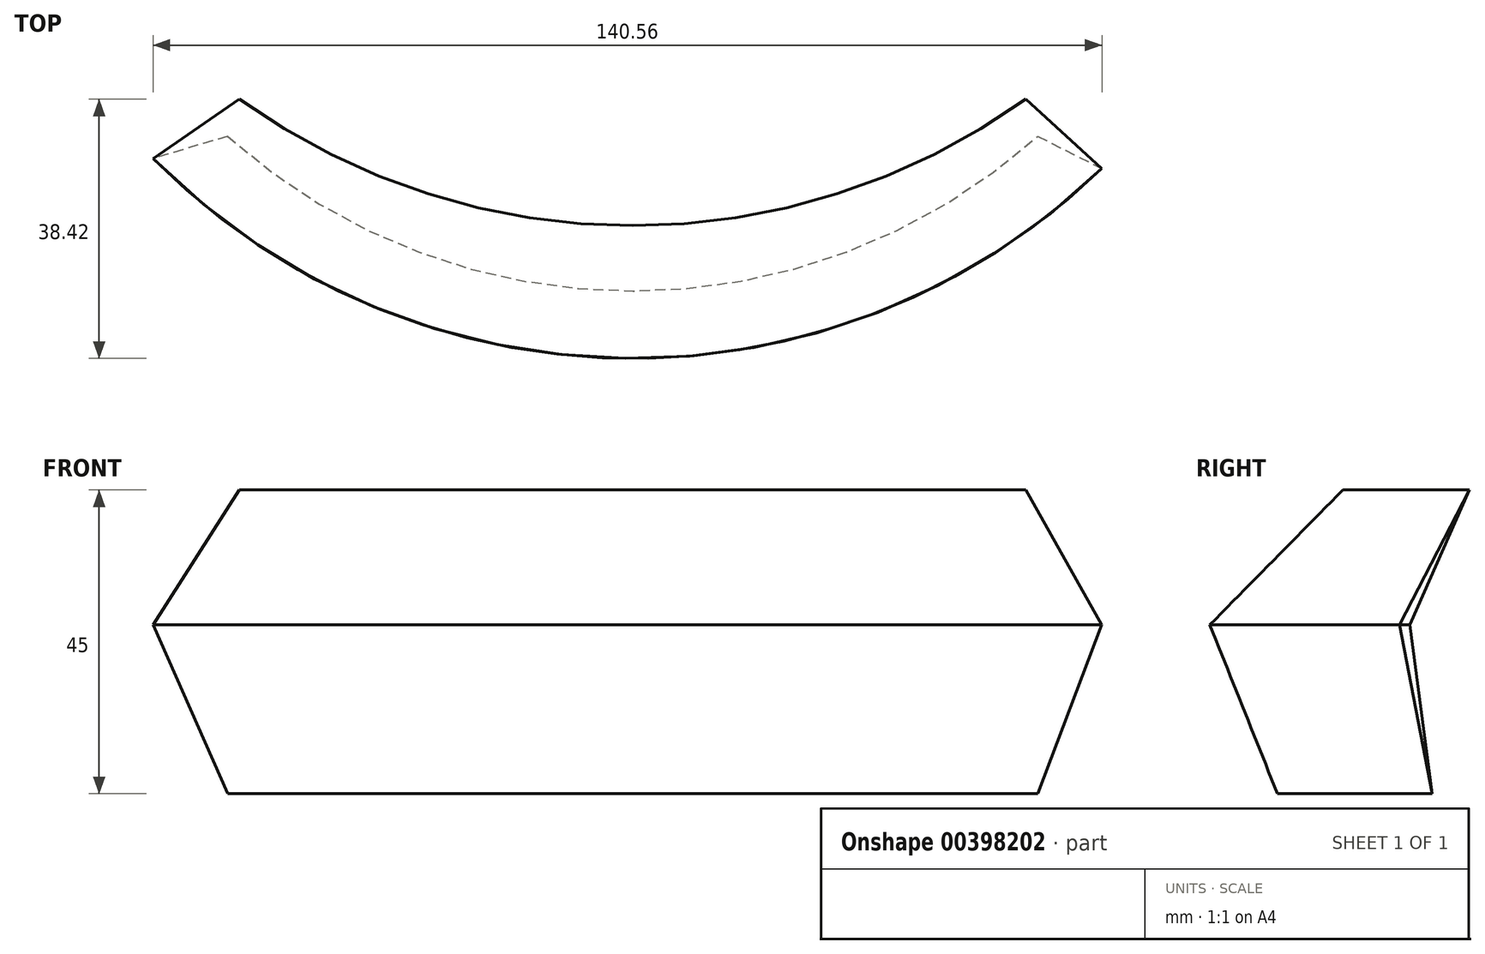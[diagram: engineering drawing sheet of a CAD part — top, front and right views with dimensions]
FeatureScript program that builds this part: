
annotation { "Feature Type Name" : "Feature", "Feature Type Description" : "" }
export const myFeature = defineFeature(function(context is Context, id is Id, definition is map)
    precondition{}
    {
        {
            var Q0;
            Q0=qCreatedBy(makeId("Top.planeOp"),FACE);
            var sketch = newSketch(context, id + "F0", { "sketchPlane" : qUnion([Q0])});
            skArc(sketch, "E0", {"start": v(-60, -67.08) * mm, "mid": v(0, -90) * mm, "end": v(60, -67.08) * mm});
            skSolve(sketch);
        }
        {
            var Q0;
            Q0=qCreatedBy(makeId("Top.planeOp"),FACE);
            cPlane(context, id + "F1", {"entities" : qUnion([Q0]), "cplaneType" : CPlaneType.OFFSET, "offset" : 25 * mm, "width" : 150 * mm, "height" : 150 * mm});
        }
        {
            var Q0;
            Q0=qCreatedBy(id+"F1.planeOp",FACE);
            var sketch = newSketch(context, id + "F2", { "sketchPlane" : qUnion([Q0])});
            skArc(sketch, "E1", {"start": v(-71.04, -70.38) * mm, "mid": v(-1.07, -100) * mm, "end": v(69.52, -71.88) * mm});
            skSolve(sketch);
        }
        {
            var Q0;
            Q0=sQuery(id+"F0.wireOp",EDGE,"E0");
            var Q1;
            Q1=sQuery(id+"F2.wireOp",EDGE,"E1");
            loft(context, id + "F3", {"bodyType" : ToolBodyType.SURFACE, "wireProfilesArray" : [{ "wireProfileEntities" : qUnion([Q0]) }, { "wireProfileEntities" : qUnion([Q1]) }]});
        }
        {
            var Q0;
            Q0=qCreatedBy(id+"F1.planeOp",FACE);
            cPlane(context, id + "F4", {"entities" : qUnion([Q0]), "cplaneType" : CPlaneType.OFFSET, "offset" : 20 * mm, "width" : 150 * mm, "height" : 150 * mm});
        }
        {
            var Q0;
            Q0=qCreatedBy(id+"F4.planeOp",FACE);
            var sketch = newSketch(context, id + "F5", { "sketchPlane" : qUnion([Q0])});
            skArc(sketch, "E2", {"start": v(-58.28, -61.58) * mm, "mid": v(0, -80.31) * mm, "end": v(58.28, -61.58) * mm});
            skSolve(sketch);
        }
        {
            var Q0;
            Q0=makeQuery(id+"F3.opLoft","SWEPT_BODY",BODY,{"disambiguationData":[OSD([sQuery(id+"F0.wireOp",EDGE,"E0"),sQuery(id+"F2.wireOp",EDGE,"E1")])]});
            var Q1;
            Q1=makeQuery(id+"F3.opLoft","SWEPT_BODY",BODY,{"disambiguationData":[OSD([sQuery(id+"F0.wireOp",EDGE,"E0"),sQuery(id+"F2.wireOp",EDGE,"E1")])]});
            var Q2;
            Q2=makeQuery(id+"F3.opLoft","MID_CAP_EDGE",EDGE,{"disambiguationData":[OSD([sQuery(id+"F2.wireOp",VERTEX,"E1.start"),sQuery(id+"F2.wireOp",VERTEX,"E1.end"),sQuery(id+"F2.wireOp",EDGE,"E1")])],"capPos":1.0});
            var Q3;
            Q3=sQuery(id+"F5.wireOp",EDGE,"E2");
            loft(context, id + "F6", {"bodyType" : ToolBodyType.SURFACE, "sheetProfilesArray" : [{ "sheetProfileEntities" : qUnion([Q0]) }, { "sheetProfileEntities" : qUnion([Q1]) }], "wireProfilesArray" : [{ "wireProfileEntities" : qUnion([Q2]) }, { "wireProfileEntities" : qUnion([Q3]) }]});
        }
    });
